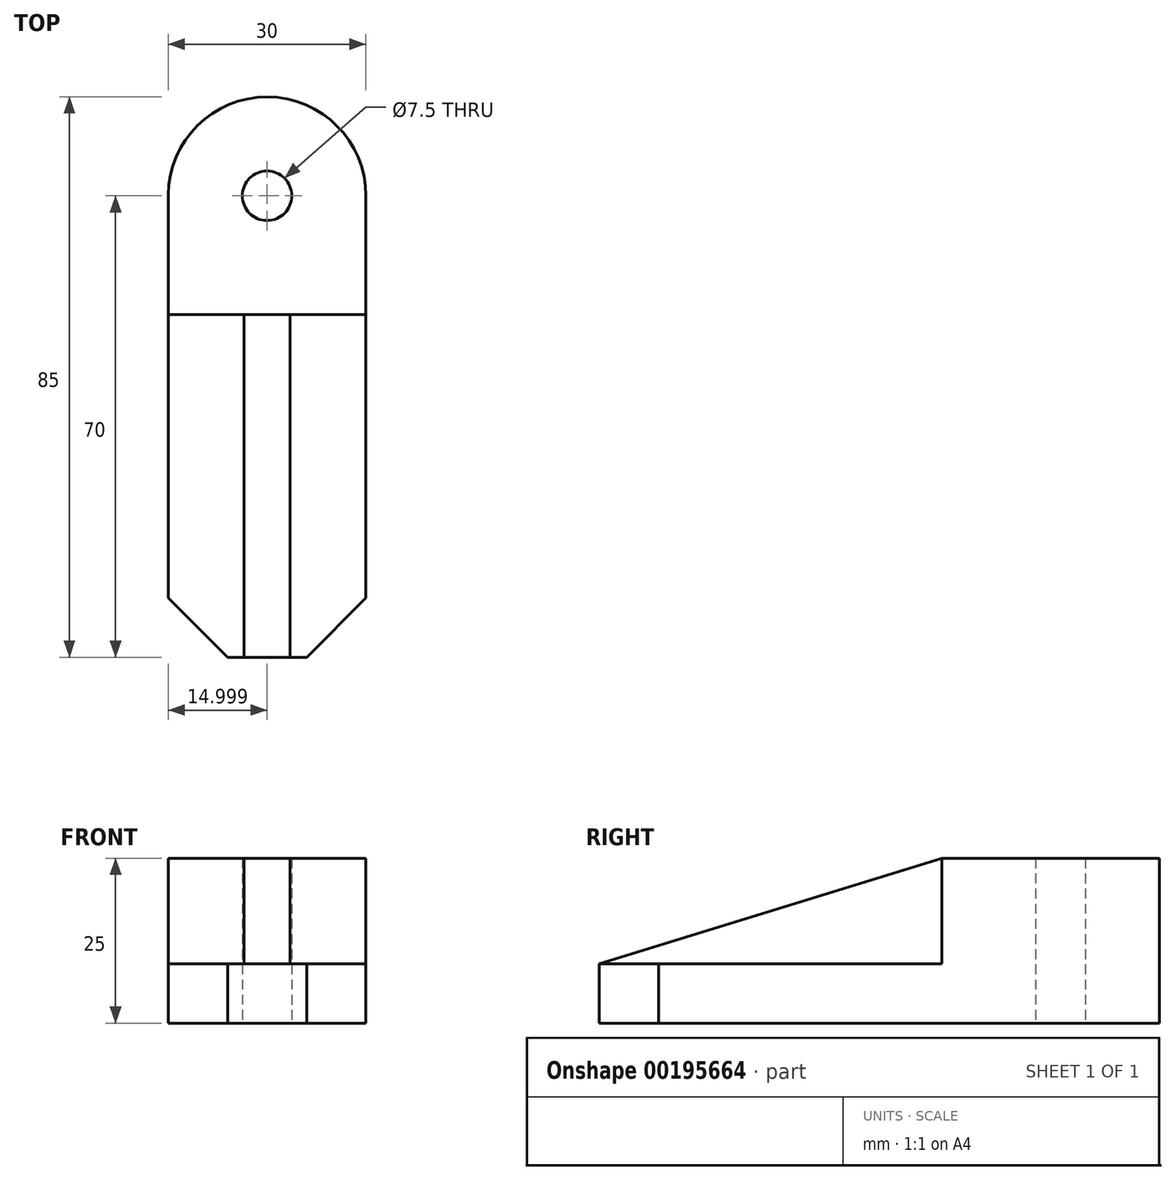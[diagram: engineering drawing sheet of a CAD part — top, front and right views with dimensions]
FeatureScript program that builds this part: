
annotation { "Feature Type Name" : "Feature", "Feature Type Description" : "" }
export const myFeature = defineFeature(function(context is Context, id is Id, definition is map)
    precondition{}
    {
        {
            var Q0;
            Q0=qCreatedBy(makeId("Top.planeOp"),FACE);
            var sketch = newSketch(context, id + "F0", { "sketchPlane" : qUnion([Q0])});
            skLineSegment(sketch, "E0.bottom", {"start": v(0, 0) * mm, "end": v(30, 0) * mm});
            skLineSegment(sketch, "E0.left", {"start": v(0, 0) * mm, "end": v(0, 18.12) * mm});
            skLineSegment(sketch, "E0.right", {"start": v(30, 0) * mm, "end": v(30, 18) * mm});
            skArc(sketch, "E1", {"start": v(30, 18) * mm, "mid": v(15.06, 33) * mm, "end": v(0, 18.12) * mm});
            skCircle(sketch, "E2", {"center": v(15, 18) * mm, "radius": 3.75 * mm});
            skSolve(sketch);
        }
        {
            var Q0;
            Q0 = qSketchRegion(id + "F0", true);
            extrude(context, id + "F1", {"entities" : qUnion([Q0]), "depth" : 25 * mm});
        }
        {
            var Q0;
            Q0=makeQuery(id+"F1.opExtrude","SWEPT_FACE",FACE,{"disambiguationData":[OSD([sQuery(id+"F0.wireOp",EDGE,"E0.bottom")])]});
            var sketch = newSketch(context, id + "F2", { "sketchPlane" : qUnion([Q0])});
            skLineSegment(sketch, "E3.bottom", {"start": v(0, 0) * mm, "end": v(30, 0) * mm});
            skLineSegment(sketch, "E3.top", {"start": v(0, 9) * mm, "end": v(30, 9) * mm});
            skLineSegment(sketch, "E3.left", {"start": v(0, 0) * mm, "end": v(0, 9) * mm});
            skLineSegment(sketch, "E3.right", {"start": v(30, 0) * mm, "end": v(30, 9) * mm});
            skSolve(sketch);
        }
        {
            var Q0;
            Q0 = qSketchRegion(id + "F2", true);
            extrude(context, id + "F3", {"entities" : qUnion([Q0]), "operationType" : NewBodyOperationType.ADD, "depth" : 52 * mm});
        }
        {
            var Q0;
            Q0=makeQuery(id+"F3.opExtrude","SWEPT_FACE",FACE,{"disambiguationData":[OSD([sQuery(id+"F2.wireOp",EDGE,"E3.top")])]});
            var sketch = newSketch(context, id + "F4", { "sketchPlane" : qUnion([Q0])});
            skLineSegment(sketch, "E4", {"start": v(30, -52) * mm, "end": v(30, -43) * mm});
            skLineSegment(sketch, "E5", {"start": v(30, -43) * mm, "end": v(21, -52) * mm});
            skLineSegment(sketch, "E6", {"start": v(21, -52) * mm, "end": v(30, -52) * mm});
            skLineSegment(sketch, "E7", {"start": v(0, -52) * mm, "end": v(9, -52) * mm});
            skLineSegment(sketch, "E8", {"start": v(9, -52) * mm, "end": v(0, -43) * mm});
            skLineSegment(sketch, "E9", {"start": v(0, -43) * mm, "end": v(0, -52) * mm});
            skSolve(sketch);
        }
        {
            var Q0;
            Q0 = qSketchRegion(id + "F4", true);
            extrude(context, id + "F5", {"entities" : qUnion([Q0]), "operationType" : NewBodyOperationType.REMOVE, "oppositeDirection" : true, "depth" : 25 * mm});
        }
        {
            var Q0;
            Q0=makeQuery(id+"F3.boolean.opBoolean","MERGE",FACE,{"derivedFrom":[makeQuery(id+"F1.opExtrude","SWEPT_FACE",FACE,{"disambiguationData":[OSD([sQuery(id+"F0.wireOp",EDGE,"E0.right")])]}),makeQuery(id+"F3.opExtrude","SWEPT_FACE",FACE,{"disambiguationData":[OSD([sQuery(id+"F2.wireOp",EDGE,"E3.right")])]})]});
            var Q1;
            Q1=makeQuery(id+"F3.boolean.opBoolean","MERGE",FACE,{"derivedFrom":[makeQuery(id+"F1.opExtrude","SWEPT_FACE",FACE,{"disambiguationData":[OSD([sQuery(id+"F0.wireOp",EDGE,"E0.left")])]}),makeQuery(id+"F3.opExtrude","SWEPT_FACE",FACE,{"disambiguationData":[OSD([sQuery(id+"F2.wireOp",EDGE,"E3.left")])]})]});
            cPlane(context, id + "F6", {"entities" : qUnion([Q0, Q1]), "cplaneType" : CPlaneType.MID_PLANE, "offset" : 25 * mm, "width" : 150 * mm, "height" : 150 * mm});
        }
        {
            var Q0;
            Q0=qCreatedBy(id+"F6.planeOp",FACE);
            var sketch = newSketch(context, id + "F7", { "sketchPlane" : qUnion([Q0])});
            skLineSegment(sketch, "E10", {"start": v(0, 25) * mm, "end": v(-52, 9) * mm});
            skLineSegment(sketch, "E11", {"start": v(-52, 9) * mm, "end": v(0, 9) * mm});
            skLineSegment(sketch, "E12", {"start": v(0, 9) * mm, "end": v(0, 25) * mm});
            skSolve(sketch);
        }
        {
            var Q0;
            Q0 = qSketchRegion(id + "F7", true);
            extrude(context, id + "F8", {"entities" : qUnion([Q0]), "operationType" : NewBodyOperationType.ADD, "depth" : 3.5 * mm, "hasSecondDirection" : true, "secondDirectionOppositeDirection" : true, "secondDirectionDepth" : 3.5 * mm});
        }
    });
